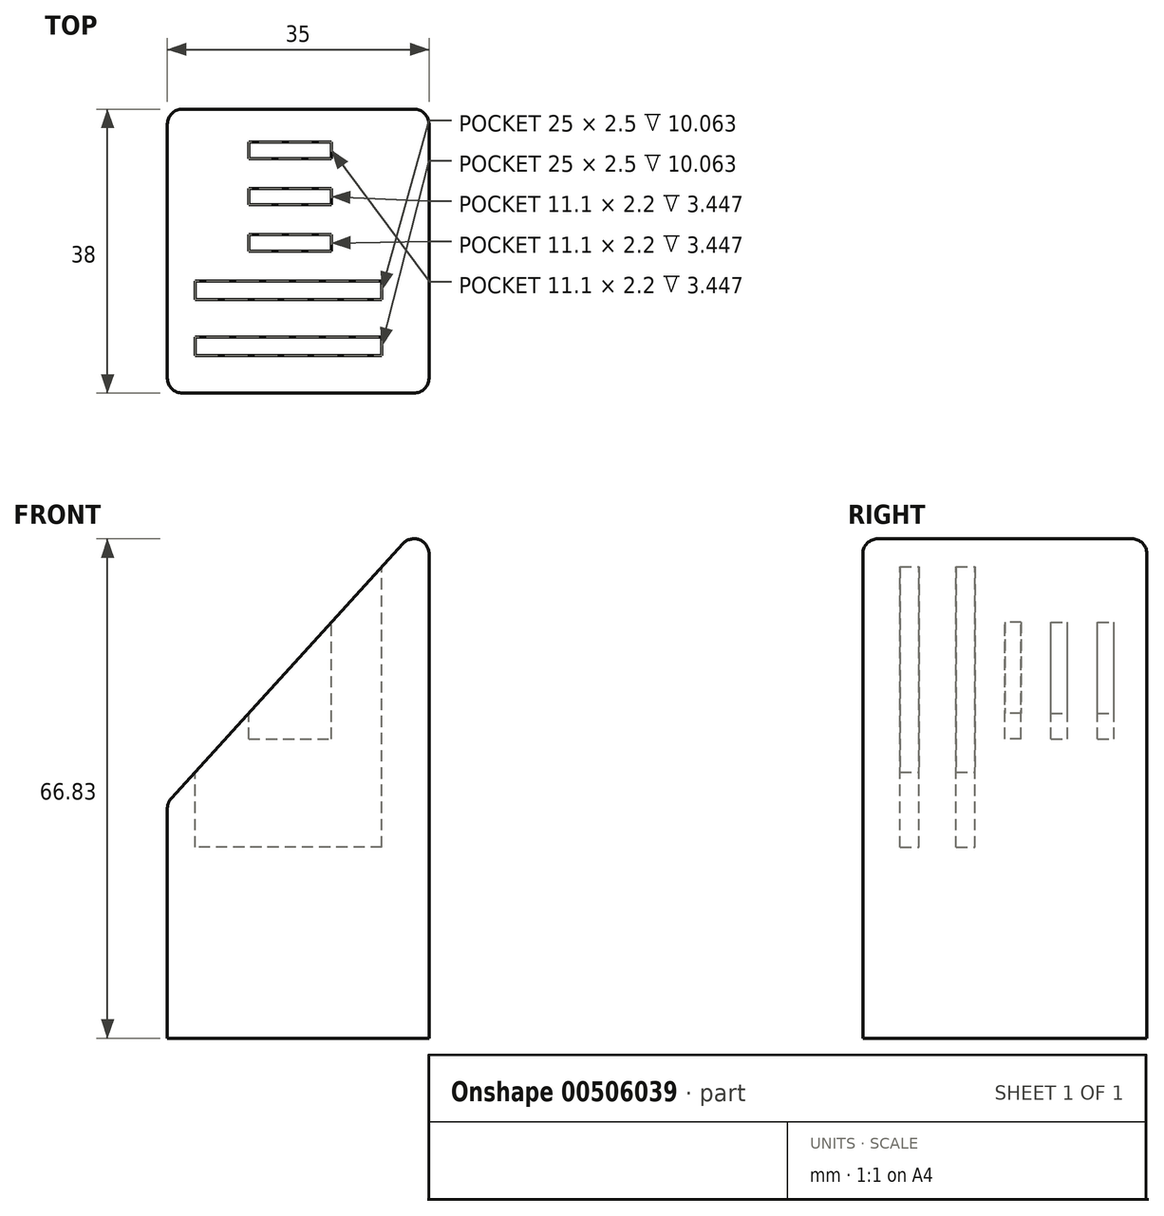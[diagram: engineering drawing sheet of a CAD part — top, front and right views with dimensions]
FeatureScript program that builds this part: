
annotation { "Feature Type Name" : "Feature", "Feature Type Description" : "" }
export const myFeature = defineFeature(function(context is Context, id is Id, definition is map)
    precondition{}
    {
        {
            var Q0;
            Q0=qCreatedBy(makeId("Front.planeOp"),FACE);
            var sketch = newSketch(context, id + "F0", { "sketchPlane" : qUnion([Q0])});
            skLineSegment(sketch, "E0", {"start": v(0, 38.46) * mm, "end": v(0, -31.54) * mm});
            skLineSegment(sketch, "E1", {"start": v(0, -31.54) * mm, "end": v(-35, -31.54) * mm});
            skLineSegment(sketch, "E2", {"start": v(-35, -31.54) * mm, "end": v(-35, 0) * mm});
            skLineSegment(sketch, "E3", {"start": v(-35, 0) * mm, "end": v(0, 38.46) * mm});
            skSolve(sketch);
        }
        {
            var Q0;
            Q0=makeQuery(id+"F0.imprint","IMPRINT",FACE,{"disambiguationData":[TD([[makeQuery(id+"F0.imprint","IMPRINT",EDGE,{"derivedFrom":sQuery(id+"F0.wireOp",EDGE,"E0")}),-1.0]])]});
            extrude(context, id + "F1", {"entities" : qUnion([Q0]), "depth" : 38 * mm});
        }
        {
            var Q0;
            Q0=qCreatedBy(makeId("Top.planeOp"),FACE);
            cPlane(context, id + "F2", {"entities" : qUnion([Q0]), "cplaneType" : CPlaneType.OFFSET, "offset" : 39 * mm, "width" : 150 * mm, "height" : 150 * mm});
        }
        {
            var Q0;
            Q0=qCreatedBy(id+"F2.planeOp",FACE);
            var sketch = newSketch(context, id + "F3", { "sketchPlane" : qUnion([Q0])});
            skLineSegment(sketch, "E4.bottom", {"start": v(-6.3, -33) * mm, "end": v(-6.3, -30.5) * mm});
            skLineSegment(sketch, "E4.top", {"start": v(-31.3, -33) * mm, "end": v(-31.3, -30.5) * mm});
            skLineSegment(sketch, "E4.left", {"start": v(-6.3, -33) * mm, "end": v(-31.3, -33) * mm});
            skLineSegment(sketch, "E4.right", {"start": v(-6.3, -30.5) * mm, "end": v(-31.3, -30.5) * mm});
            skLineSegment(sketch, "E5.bottom", {"start": v(-6.3, -25.5) * mm, "end": v(-6.3, -23) * mm});
            skLineSegment(sketch, "E5.top", {"start": v(-31.3, -25.5) * mm, "end": v(-31.3, -23) * mm});
            skLineSegment(sketch, "E5.left", {"start": v(-6.3, -25.5) * mm, "end": v(-31.3, -25.5) * mm});
            skLineSegment(sketch, "E5.right", {"start": v(-6.3, -23) * mm, "end": v(-31.3, -23) * mm});
            skLineSegment(sketch, "E6.bottom", {"start": v(-13.03, -16.8) * mm, "end": v(-13.03, -19) * mm});
            skLineSegment(sketch, "E6.top", {"start": v(-24.13, -16.8) * mm, "end": v(-24.13, -19) * mm});
            skLineSegment(sketch, "E6.left", {"start": v(-13.03, -16.8) * mm, "end": v(-24.13, -16.8) * mm});
            skLineSegment(sketch, "E6.right", {"start": v(-13.03, -19) * mm, "end": v(-24.13, -19) * mm});
            skPoint(sketch, "E6.middle", {"position": v(-18.58, -17.9) * mm});
            skLineSegment(sketch, "E7.bottom", {"start": v(-24.13, -12.8) * mm, "end": v(-24.13, -10.6) * mm});
            skLineSegment(sketch, "E7.top", {"start": v(-13.03, -12.8) * mm, "end": v(-13.03, -10.6) * mm});
            skLineSegment(sketch, "E7.left", {"start": v(-24.13, -12.8) * mm, "end": v(-13.03, -12.8) * mm});
            skLineSegment(sketch, "E7.right", {"start": v(-24.13, -10.6) * mm, "end": v(-13.03, -10.6) * mm});
            skPoint(sketch, "E7.middle", {"position": v(-18.58, -11.7) * mm});
            skLineSegment(sketch, "E8.bottom", {"start": v(-24.13, -6.6) * mm, "end": v(-24.13, -4.4) * mm});
            skLineSegment(sketch, "E8.top", {"start": v(-13.03, -6.6) * mm, "end": v(-13.03, -4.4) * mm});
            skLineSegment(sketch, "E8.left", {"start": v(-24.13, -6.6) * mm, "end": v(-13.03, -6.6) * mm});
            skLineSegment(sketch, "E8.right", {"start": v(-24.13, -4.4) * mm, "end": v(-13.03, -4.4) * mm});
            skPoint(sketch, "E8.middle", {"position": v(-18.58, -5.5) * mm});
            skSolve(sketch);
        }
        {
            var Q0;
            Q0=makeQuery(id+"F3.imprint","IMPRINT",FACE,{"disambiguationData":[TD([[makeQuery(id+"F3.imprint","IMPRINT",EDGE,{"derivedFrom":sQuery(id+"F3.wireOp",EDGE,"E4.bottom")}),1.0]])]});
            var Q1;
            Q1=makeQuery(id+"F3.imprint","IMPRINT",FACE,{"disambiguationData":[TD([[makeQuery(id+"F3.imprint","IMPRINT",EDGE,{"derivedFrom":sQuery(id+"F3.wireOp",EDGE,"E5.bottom")}),1.0]])]});
            extrude(context, id + "F4", {"entities" : qUnion([Q0, Q1]), "operationType" : NewBodyOperationType.REMOVE, "oppositeDirection" : true, "depth" : 45 * mm});
        }
        {
            var Q0;
            Q0=makeQuery(id+"F3.imprint","IMPRINT",FACE,{"disambiguationData":[TD([[makeQuery(id+"F3.imprint","IMPRINT",EDGE,{"derivedFrom":sQuery(id+"F3.wireOp",EDGE,"E7.bottom")}),-1.0]])]});
            var Q1;
            Q1=makeQuery(id+"F3.imprint","IMPRINT",FACE,{"disambiguationData":[TD([[makeQuery(id+"F3.imprint","IMPRINT",EDGE,{"derivedFrom":sQuery(id+"F3.wireOp",EDGE,"E6.bottom")}),-1.0]])]});
            var Q2;
            Q2=makeQuery(id+"F3.imprint","IMPRINT",FACE,{"disambiguationData":[TD([[makeQuery(id+"F3.imprint","IMPRINT",EDGE,{"derivedFrom":sQuery(id+"F3.wireOp",EDGE,"E8.bottom")}),-1.0]])]});
            extrude(context, id + "F5", {"entities" : qUnion([Q0, Q1, Q2]), "operationType" : NewBodyOperationType.REMOVE, "oppositeDirection" : true, "depth" : 30.5 * mm});
        }
        {
            var Q0;
            Q0=makeQuery(id+"F1.opExtrude","CAP_EDGE",EDGE,{"disambiguationData":[OSD([sQuery(id+"F0.wireOp",EDGE,"E3")])],"isStart":true});
            var Q1;
            Q1=makeQuery(id+"F1.opExtrude","SWEPT_EDGE",EDGE,{"disambiguationData":[OSD([sQuery(id+"F0.wireOp",EDGE,"E2"),sQuery(id+"F0.wireOp",EDGE,"E3")])]});
            var Q2;
            Q2=makeQuery(id+"F1.opExtrude","CAP_EDGE",EDGE,{"disambiguationData":[OSD([sQuery(id+"F0.wireOp",EDGE,"E3")])],"isStart":false});
            var Q3;
            Q3=makeQuery(id+"F1.opExtrude","SWEPT_EDGE",EDGE,{"disambiguationData":[OSD([sQuery(id+"F0.wireOp",EDGE,"E0"),sQuery(id+"F0.wireOp",EDGE,"E3")])]});
            var Q4;
            Q4=makeQuery(id+"F1.opExtrude","CAP_EDGE",EDGE,{"disambiguationData":[OSD([sQuery(id+"F0.wireOp",EDGE,"E0")])],"isStart":true});
            var Q5;
            Q5=makeQuery(id+"F1.opExtrude","CAP_EDGE",EDGE,{"disambiguationData":[OSD([sQuery(id+"F0.wireOp",EDGE,"E0")])],"isStart":false});
            var Q6;
            Q6=makeQuery(id+"F1.opExtrude","CAP_EDGE",EDGE,{"disambiguationData":[OSD([sQuery(id+"F0.wireOp",EDGE,"E2")])],"isStart":true});
            var Q7;
            Q7=makeQuery(id+"F1.opExtrude","CAP_EDGE",EDGE,{"disambiguationData":[OSD([sQuery(id+"F0.wireOp",EDGE,"E2")])],"isStart":false});
            fillet(context, id + "F6", {"entities" : qUnion([Q0, Q1, Q2, Q3, Q4, Q5, Q6, Q7]), "radius" : 2 * mm, "tangentPropagation" : true, "allowEdgeOverflow" : false});
        }
    });
